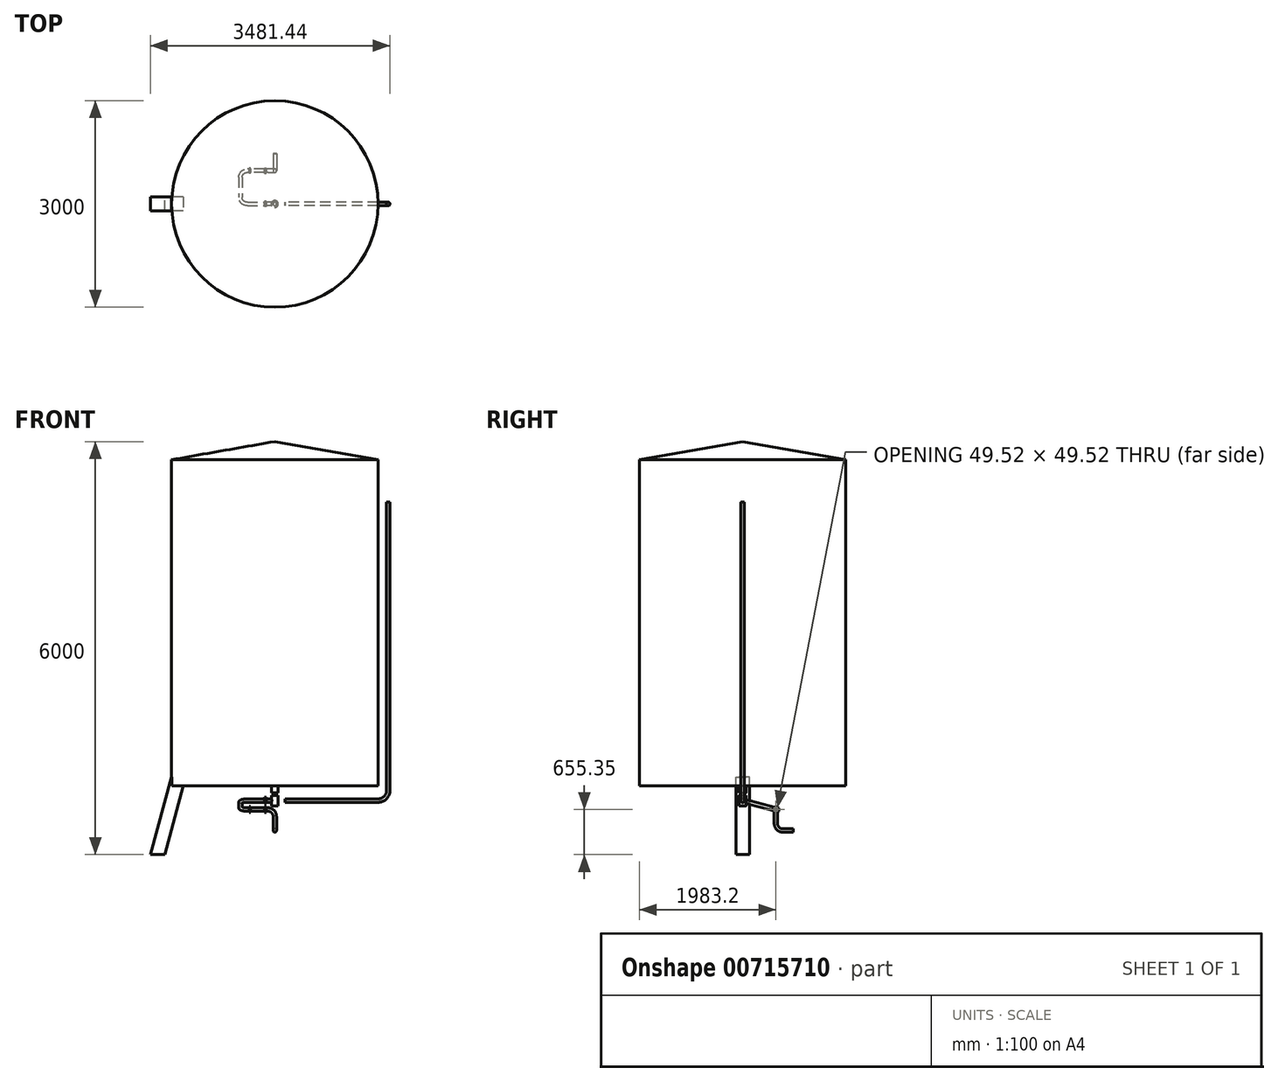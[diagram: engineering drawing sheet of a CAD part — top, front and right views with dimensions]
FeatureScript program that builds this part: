
annotation { "Feature Type Name" : "Feature", "Feature Type Description" : "" }
export const myFeature = defineFeature(function(context is Context, id is Id, definition is map)
    precondition{}
    {
        {
            var Q0;
            Q0=qCreatedBy(makeId("Front.planeOp"),FACE);
            var sketch = newSketch(context, id + "F0", { "sketchPlane" : qUnion([Q0])});
            skLineSegment(sketch, "E0", {"start": v(0, 5290) * mm, "end": v(0, 0) * mm});
            skLineSegment(sketch, "E1", {"start": v(0, 5290) * mm, "end": v(-1500, 5025.5) * mm});
            skLineSegment(sketch, "E2", {"start": v(-1500, 5025.5) * mm, "end": v(-1500, 290) * mm});
            skLineSegment(sketch, "E3", {"start": v(-1500, 290) * mm, "end": v(-50, 290) * mm});
            skLineSegment(sketch, "E4", {"start": v(-50, 290) * mm, "end": v(-50, 190) * mm});
            skLineSegment(sketch, "E5", {"start": v(-25, 190) * mm, "end": v(-50, 190) * mm});
            skLineSegment(sketch, "E6", {"start": v(-50, 0) * mm, "end": v(0, 0) * mm});
            skLineSegment(sketch, "E7", {"start": v(-50, 150) * mm, "end": v(-50, 0) * mm});
            skLineSegment(sketch, "E8", {"start": v(-25, 190) * mm, "end": v(-25, 150) * mm});
            skLineSegment(sketch, "E9", {"start": v(-25, 150) * mm, "end": v(-50, 150) * mm});
            skSolve(sketch);
        }
        {
            var Q0;
            Q0=makeQuery(id+"F0.imprint","IMPRINT",FACE,{"disambiguationData":[TD([[makeQuery(id+"F0.imprint","IMPRINT",EDGE,{"derivedFrom":sQuery(id+"F0.wireOp",EDGE,"E0")}),-1.0]])]});
            var Q1;
            Q1=sQuery(id+"F0.wireOp",EDGE,"E0");
            revolve(context, id + "F1", {"surfaceOperationType" : NewSurfaceOperationType.NEW, "entities" : qUnion([Q0]), "axis" : qUnion([Q1]), "revolveType" : RevolveType.FULL});
        }
        {
            var Q0;
            Q0=qCreatedBy(makeId("Front.planeOp"),FACE);
            var sketch = newSketch(context, id + "F2", { "sketchPlane" : qUnion([Q0])});
            skLineSegment(sketch, "E10", {"start": v(-1500, 5025.5) * mm, "end": v(-1500, 290) * mm, "construction": true});
            skLineSegment(sketch, "E11", {"start": v(1500, 290) * mm, "end": v(1500, 5025.5) * mm});
            skLineSegment(sketch, "E12", {"start": v(50, 290) * mm, "end": v(1500, 290) * mm});
            skLineSegment(sketch, "E13", {"start": v(-1500, 290) * mm, "end": v(-50, 290) * mm, "construction": true});
            skLineSegment(sketch, "E14", {"start": v(-1806.44, -710) * mm, "end": v(-1505, 415) * mm});
            skLineSegment(sketch, "E15", {"start": v(-1297.94, 415) * mm, "end": v(-1599.39, -710) * mm});
            skLineSegment(sketch, "E16", {"start": v(-1599.39, -710) * mm, "end": v(-1806.44, -710) * mm});
            skLineSegment(sketch, "E17", {"start": v(-1505, 415) * mm, "end": v(-1297.94, 415) * mm});
            skSolve(sketch);
        }
        {
            var Q0;
            Q0=makeQuery(id+"F2.imprint","IMPRINT",FACE,{"disambiguationData":[TD([[makeQuery(id+"F2.imprint","IMPRINT",EDGE,{"derivedFrom":sQuery(id+"F2.wireOp",EDGE,"E14")}),-1.0]])]});
            extrude(context, id + "F3", {"entities" : qUnion([Q0]), "operationType" : NewBodyOperationType.ADD, "endBound" : BoundingType.SYMMETRIC, "depth" : 200 * mm, "offsetDistance" : 25 * mm});
        }
        {
            var Q0;
            Q0=qCreatedBy(makeId("Right.planeOp"),FACE);
            cPlane(context, id + "F4", {"entities" : qUnion([Q0]), "cplaneType" : CPlaneType.OFFSET, "offset" : 150 * mm, "oppositeDirection" : true, "width" : 150 * mm, "height" : 150 * mm});
        }
        {
            var Q0;
            Q0=qCreatedBy(id+"F4.planeOp",FACE);
            var sketch = newSketch(context, id + "F5", { "sketchPlane" : qUnion([Q0])});
            skLineSegment(sketch, "E18", {"start": v(0, 0) * mm, "end": v(0, 150) * mm, "construction": true});
            skLineSegment(sketch, "E19.0", {"start": v(-50, 150) * mm, "end": v(50, 150) * mm, "construction": true});
            skLineSegment(sketch, "E20.0", {"start": v(-50, 0) * mm, "end": v(50, 0) * mm, "construction": true});
            skCircle(sketch, "E21", {"center": v(0, 75) * mm, "radius": 25 * mm});
            skCircle(sketch, "E22.cCircle", {"center": v(0, 75) * mm, "radius": 40 * mm, "construction": true});
            skLineSegment(sketch, "E22.0", {"start": v(-40, 51.9) * mm, "end": v(-40, 98.1) * mm});
            skLineSegment(sketch, "E22.1", {"start": v(-40, 98.1) * mm, "end": v(0, 121.19) * mm});
            skLineSegment(sketch, "E22.2", {"start": v(0, 121.19) * mm, "end": v(40, 98.1) * mm});
            skLineSegment(sketch, "E22.3", {"start": v(40, 98.1) * mm, "end": v(40, 51.9) * mm});
            skLineSegment(sketch, "E22.4", {"start": v(40, 51.9) * mm, "end": v(0, 28.81) * mm});
            skLineSegment(sketch, "E22.5", {"start": v(0, 28.81) * mm, "end": v(-40, 51.9) * mm});
            skPoint(sketch, "E22.0.midPoint", {"position": v(-40, 75) * mm});
            skSolve(sketch);
        }
        {
            var Q0;
            Q0=makeQuery(id+"F5.imprint","IMPRINT",FACE,{"disambiguationData":[TD([[makeQuery(id+"F5.imprint","IMPRINT",EDGE,{"derivedFrom":sQuery(id+"F5.wireOp",EDGE,"E21")}),-1.0]])]});
            var Q1;
            Q1=makeQuery(id+"F5.imprint","IMPRINT",FACE,{"disambiguationData":[TD([[makeQuery(id+"F5.imprint","IMPRINT",EDGE,{"derivedFrom":sQuery(id+"F5.wireOp",EDGE,"E21")}),1.0]])]});
            extrude(context, id + "F6", {"entities" : qUnion([Q0, Q1]), "depth" : 25 * mm, "offsetDistance" : 25 * mm});
        }
        {
            var Q0;
            Q0=makeQuery(id+"F5.imprint","IMPRINT",FACE,{"disambiguationData":[TD([[makeQuery(id+"F5.imprint","IMPRINT",EDGE,{"derivedFrom":sQuery(id+"F5.wireOp",EDGE,"E21")}),1.0]])]});
            var Q1;
            Q1=makeQuery(id+"F1.opRevolve","SWEPT_FACE",FACE,{"disambiguationData":[OSD([sQuery(id+"F0.wireOp",EDGE,"E7")])]});
            extrude(context, id + "F7", {"entities" : qUnion([Q0]), "operationType" : NewBodyOperationType.ADD, "endBound" : BoundingType.UP_TO_SURFACE, "depth" : 25 * mm, "endBoundEntityFace" : qUnion([Q1]), "offsetDistance" : 25 * mm});
        }
        {
            var Q0;
            Q0=qCreatedBy(makeId("Front.planeOp"),FACE);
            var sketch = newSketch(context, id + "F8", { "sketchPlane" : qUnion([Q0])});
            skLineSegment(sketch, "E23.0.0", {"start": v(150, 51.9) * mm, "end": v(150, 28.81) * mm, "construction": true});
            skLineSegment(sketch, "E23.0.1", {"start": v(150, 28.81) * mm, "end": v(150, 51.9) * mm, "construction": true});
            skLineSegment(sketch, "E23.0.2", {"start": v(150, 51.9) * mm, "end": v(150, 98.1) * mm, "construction": true});
            skLineSegment(sketch, "E23.0.3", {"start": v(150, 98.1) * mm, "end": v(150, 121.19) * mm, "construction": true});
            skLineSegment(sketch, "E23.0.4", {"start": v(150, 121.19) * mm, "end": v(150, 98.1) * mm, "construction": true});
            skLineSegment(sketch, "E23.0.5", {"start": v(150, 98.1) * mm, "end": v(150, 51.9) * mm, "construction": true});
            skLineSegment(sketch, "E24", {"start": v(150, 75) * mm, "end": v(1500, 75) * mm});
            skLineSegment(sketch, "E25", {"start": v(1650, 225) * mm, "end": v(1650, 4408.12) * mm});
            skPoint(sketch, "E26.visualSharp", {"position": v(1650, 75) * mm});
            skArc(sketch, "E26.filletArc", {"start": v(1500, 75) * mm, "mid": v(1606.07, 118.93) * mm, "end": v(1650, 225) * mm});
            skSolve(sketch);
        }
        {
            var Q0;
            Q0=makeQuery(id+"F7.opExtrude","SWEPT_FACE",FACE,{"disambiguationData":[OSD([sQuery(id+"F5.wireOp",EDGE,"E21")])]});
            var Q1;
            Q1=qCreatedBy(makeId("Top.planeOp"),FACE);
            cPlane(context, id + "F9", {"entities" : qUnion([Q0, Q1]), "cplaneType" : CPlaneType.LINE_ANGLE, "offset" : 25 * mm, "angle" : 15 * degree, "width" : 150 * mm, "height" : 150 * mm});
        }
        {
            var Q0;
            Q0=qCreatedBy(id+"F9.planeOp",FACE);
            var sketch = newSketch(context, id + "F10", { "sketchPlane" : qUnion([Q0])});
            skPoint(sketch, "E27.0", {"position": v(-150, 19.41) * mm});
            skLineSegment(sketch, "E28", {"start": v(-150, 19.41) * mm, "end": v(-400, 19.41) * mm});
            skLineSegment(sketch, "E29", {"start": v(-500, -80.59) * mm, "end": v(-500, -380.59) * mm});
            skLineSegment(sketch, "E30", {"start": v(-400, -480.59) * mm, "end": v(-375, -480.59) * mm});
            skPoint(sketch, "E31.visualSharp", {"position": v(-500, 19.41) * mm});
            skArc(sketch, "E31.filletArc", {"start": v(-400, 19.41) * mm, "mid": v(-470.71, -9.88) * mm, "end": v(-500, -80.59) * mm});
            skPoint(sketch, "E32.visualSharp", {"position": v(-500, -480.59) * mm});
            skArc(sketch, "E32.filletArc", {"start": v(-500, -380.59) * mm, "mid": v(-470.71, -451.3) * mm, "end": v(-400, -480.59) * mm});
            skSolve(sketch);
        }
        {
            var Q0;
            Q0=qCreatedBy(makeId("Front.planeOp"),FACE);
            var Q1;
            Q1=sQuery(id+"F10.wireOp",VERTEX,"E30.end");
            cPlane(context, id + "F11", {"entities" : qUnion([Q0, Q1]), "cplaneType" : CPlaneType.PLANE_POINT, "offset" : 25 * mm, "width" : 150 * mm, "height" : 150 * mm});
        }
        {
            var Q0;
            Q0=qCreatedBy(id+"F11.planeOp",FACE);
            var sketch = newSketch(context, id + "F12", { "sketchPlane" : qUnion([Q0])});
            skLineSegment(sketch, "E33", {"start": v(0, -154.4) * mm, "end": v(0, -204.4) * mm});
            skPoint(sketch, "E34.0", {"position": v(-375, -54.4) * mm});
            skLineSegment(sketch, "E35", {"start": v(-375, -54.4) * mm, "end": v(-100, -54.4) * mm});
            skPoint(sketch, "E36.visualSharp", {"position": v(0, -54.4) * mm});
            skArc(sketch, "E36.filletArc", {"start": v(0, -154.4) * mm, "mid": v(-29.29, -83.7) * mm, "end": v(-100, -54.4) * mm});
            skPoint(sketch, "E37", {"position": v(-125, -54.4) * mm});
            skSolve(sketch);
        }
        {
            var Q0;
            Q0=qCreatedBy(makeId("Right.planeOp"),FACE);
            var sketch = newSketch(context, id + "F13", { "sketchPlane" : qUnion([Q0])});
            skLineSegment(sketch, "E38", {"start": v(582.96, -360) * mm, "end": v(732.96, -360) * mm});
            skPoint(sketch, "E39.0", {"position": v(482.96, -204.4) * mm});
            skLineSegment(sketch, "E40", {"start": v(482.96, -204.4) * mm, "end": v(482.96, -260) * mm});
            skPoint(sketch, "E41.visualSharp", {"position": v(482.96, -360) * mm});
            skArc(sketch, "E41.filletArc", {"start": v(482.96, -260) * mm, "mid": v(512.25, -330.71) * mm, "end": v(582.96, -360) * mm});
            skSolve(sketch);
        }
        {
            var Q0;
            Q0=sQuery(id+"F13.wireOp",VERTEX,"E38.end");
            var Q1;
            Q1=sQuery(id+"F13.wireOp",EDGE,"E38");
            cPlane(context, id + "F14", {"entities" : qUnion([Q0, Q1]), "cplaneType" : CPlaneType.LINE_POINT, "offset" : 25 * mm, "width" : 150 * mm, "height" : 150 * mm});
        }
        {
            var Q0;
            Q0=qCreatedBy(id+"F14.planeOp",FACE);
            var sketch = newSketch(context, id + "F15", { "sketchPlane" : qUnion([Q0])});
            skCircle(sketch, "E42", {"center": v(0, -360) * mm, "radius": 25 * mm});
            skSolve(sketch);
        }
        {
            var Q0;
            Q0=sQuery(id+"F8.wireOp",VERTEX,"E25.end");
            var Q1;
            Q1=sQuery(id+"F8.wireOp",EDGE,"E25");
            cPlane(context, id + "F16", {"entities" : qUnion([Q0, Q1]), "cplaneType" : CPlaneType.LINE_POINT, "offset" : 25 * mm, "width" : 150 * mm, "height" : 150 * mm});
        }
        {
            var Q0;
            Q0=qCreatedBy(id+"F16.planeOp",FACE);
            var sketch = newSketch(context, id + "F17", { "sketchPlane" : qUnion([Q0])});
            skPoint(sketch, "E43.0", {"position": v(1650, 0) * mm});
            skCircle(sketch, "E44", {"center": v(1650, 0) * mm, "radius": 25 * mm});
            skSolve(sketch);
        }
        {
            var Q0;
            Q0=makeQuery(id+"F17.imprint","IMPRINT",FACE,{"disambiguationData":[TD([[makeQuery(id+"F17.imprint","IMPRINT",EDGE,{"derivedFrom":sQuery(id+"F17.wireOp",EDGE,"E44")}),1.0]])]});
            var Q1;
            Q1=sQuery(id+"F8.wireOp",EDGE,"E25");
            var Q2;
            Q2=sQuery(id+"F8.wireOp",EDGE,"E26.filletArc");
            var Q3;
            Q3=sQuery(id+"F8.wireOp",EDGE,"E24");
            sweep(context, id + "F18", {"operationType" : NewBodyOperationType.ADD, "profiles" : qUnion([Q0]), "path" : qUnion([Q1, Q2, Q3])});
        }
        {
            var Q0;
            Q0=makeQuery(id+"F15.imprint","IMPRINT",FACE,{"disambiguationData":[TD([[makeQuery(id+"F15.imprint","IMPRINT",EDGE,{"derivedFrom":sQuery(id+"F15.wireOp",EDGE,"E42")}),1.0]])]});
            var Q1;
            Q1=sQuery(id+"F13.wireOp",EDGE,"E38");
            var Q2;
            Q2=sQuery(id+"F13.wireOp",EDGE,"E41.filletArc");
            var Q3;
            Q3=sQuery(id+"F13.wireOp",EDGE,"E40");
            var Q4;
            Q4=sQuery(id+"F12.wireOp",EDGE,"E33");
            var Q5;
            Q5=sQuery(id+"F12.wireOp",EDGE,"E36.filletArc");
            var Q6;
            Q6=sQuery(id+"F12.wireOp",EDGE,"E35");
            var Q7;
            Q7=sQuery(id+"F10.wireOp",EDGE,"E30");
            var Q8;
            Q8=sQuery(id+"F10.wireOp",EDGE,"E32.filletArc");
            var Q9;
            Q9=sQuery(id+"F10.wireOp",EDGE,"E29");
            var Q10;
            Q10=sQuery(id+"F10.wireOp",EDGE,"E31.filletArc");
            var Q11;
            Q11=sQuery(id+"F10.wireOp",EDGE,"E28");
            sweep(context, id + "F19", {"operationType" : NewBodyOperationType.ADD, "profiles" : qUnion([Q0]), "path" : qUnion([Q1, Q2, Q3, Q4, Q5, Q6, Q7, Q8, Q9, Q10, Q11])});
        }
        {
            var Q0;
            Q0=sQuery(id+"F12.wireOp",VERTEX,"E37");
            var Q1;
            Q1=sQuery(id+"F12.wireOp",EDGE,"E35");
            cPlane(context, id + "F20", {"entities" : qUnion([Q0, Q1]), "cplaneType" : CPlaneType.LINE_POINT, "offset" : 25 * mm, "width" : 150 * mm, "height" : 150 * mm});
        }
        {
            var Q0;
            Q0=qCreatedBy(id+"F20.planeOp",FACE);
            var sketch = newSketch(context, id + "F21", { "sketchPlane" : qUnion([Q0])});
            skPoint(sketch, "E45.0", {"position": v(482.96, -54.4) * mm});
            skCircle(sketch, "E46.cCircle", {"center": v(482.96, -54.4) * mm, "radius": 40 * mm, "construction": true});
            skLineSegment(sketch, "E46.0", {"start": v(522.96, -31.32) * mm, "end": v(522.96, -77.5) * mm});
            skLineSegment(sketch, "E46.1", {"start": v(522.96, -77.5) * mm, "end": v(482.96, -100.6) * mm});
            skLineSegment(sketch, "E46.2", {"start": v(482.96, -100.6) * mm, "end": v(442.96, -77.5) * mm});
            skLineSegment(sketch, "E46.3", {"start": v(442.96, -77.5) * mm, "end": v(442.96, -31.32) * mm});
            skLineSegment(sketch, "E46.4", {"start": v(442.96, -31.32) * mm, "end": v(482.96, -8.22) * mm});
            skLineSegment(sketch, "E46.5", {"start": v(482.96, -8.22) * mm, "end": v(522.96, -31.32) * mm});
            skPoint(sketch, "E46.0.midPoint", {"position": v(522.96, -54.4) * mm});
            skSolve(sketch);
        }
        {
            var Q0;
            Q0=makeQuery(id+"F21.imprint","IMPRINT",FACE,{"disambiguationData":[TD([[makeQuery(id+"F21.imprint","IMPRINT",EDGE,{"derivedFrom":sQuery(id+"F21.wireOp",EDGE,"E46.0")}),-1.0]])]});
            extrude(context, id + "F22", {"entities" : qUnion([Q0]), "operationType" : NewBodyOperationType.ADD, "oppositeDirection" : true, "depth" : 25 * mm, "offsetDistance" : 25 * mm});
        }
        {
            var Q0;
            Q0=sQuery(id+"F12.wireOp",VERTEX,"E34.0");
            var Q1;
            Q1=sQuery(id+"F12.wireOp",EDGE,"E35");
            cPlane(context, id + "F23", {"entities" : qUnion([Q0, Q1]), "cplaneType" : CPlaneType.LINE_POINT, "offset" : 25 * mm, "width" : 150 * mm, "height" : 150 * mm});
        }
        {
            var Q0;
            Q0=qCreatedBy(id+"F23.planeOp",FACE);
            var sketch = newSketch(context, id + "F24", { "sketchPlane" : qUnion([Q0])});
            skPoint(sketch, "E47.0", {"position": v(482.96, -54.4) * mm});
            skCircle(sketch, "E48.cCircle", {"center": v(482.96, -54.4) * mm, "radius": 40 * mm, "construction": true});
            skLineSegment(sketch, "E48.0", {"start": v(522.96, -31.32) * mm, "end": v(522.96, -77.5) * mm});
            skLineSegment(sketch, "E48.1", {"start": v(522.96, -77.5) * mm, "end": v(482.96, -100.6) * mm});
            skLineSegment(sketch, "E48.2", {"start": v(482.96, -100.6) * mm, "end": v(442.96, -77.5) * mm});
            skLineSegment(sketch, "E48.3", {"start": v(442.96, -77.5) * mm, "end": v(442.96, -31.32) * mm});
            skLineSegment(sketch, "E48.4", {"start": v(442.96, -31.32) * mm, "end": v(482.96, -8.22) * mm});
            skLineSegment(sketch, "E48.5", {"start": v(482.96, -8.22) * mm, "end": v(522.96, -31.32) * mm});
            skPoint(sketch, "E48.0.midPoint", {"position": v(522.96, -54.4) * mm});
            skSolve(sketch);
        }
        {
            var Q0;
            Q0=makeQuery(id+"F24.imprint","IMPRINT",FACE,{"disambiguationData":[TD([[makeQuery(id+"F24.imprint","IMPRINT",EDGE,{"derivedFrom":sQuery(id+"F24.wireOp",EDGE,"E48.0")}),-1.0]])]});
            extrude(context, id + "F25", {"entities" : qUnion([Q0]), "operationType" : NewBodyOperationType.ADD, "depth" : 25 * mm, "offsetDistance" : 25 * mm});
        }
    });
